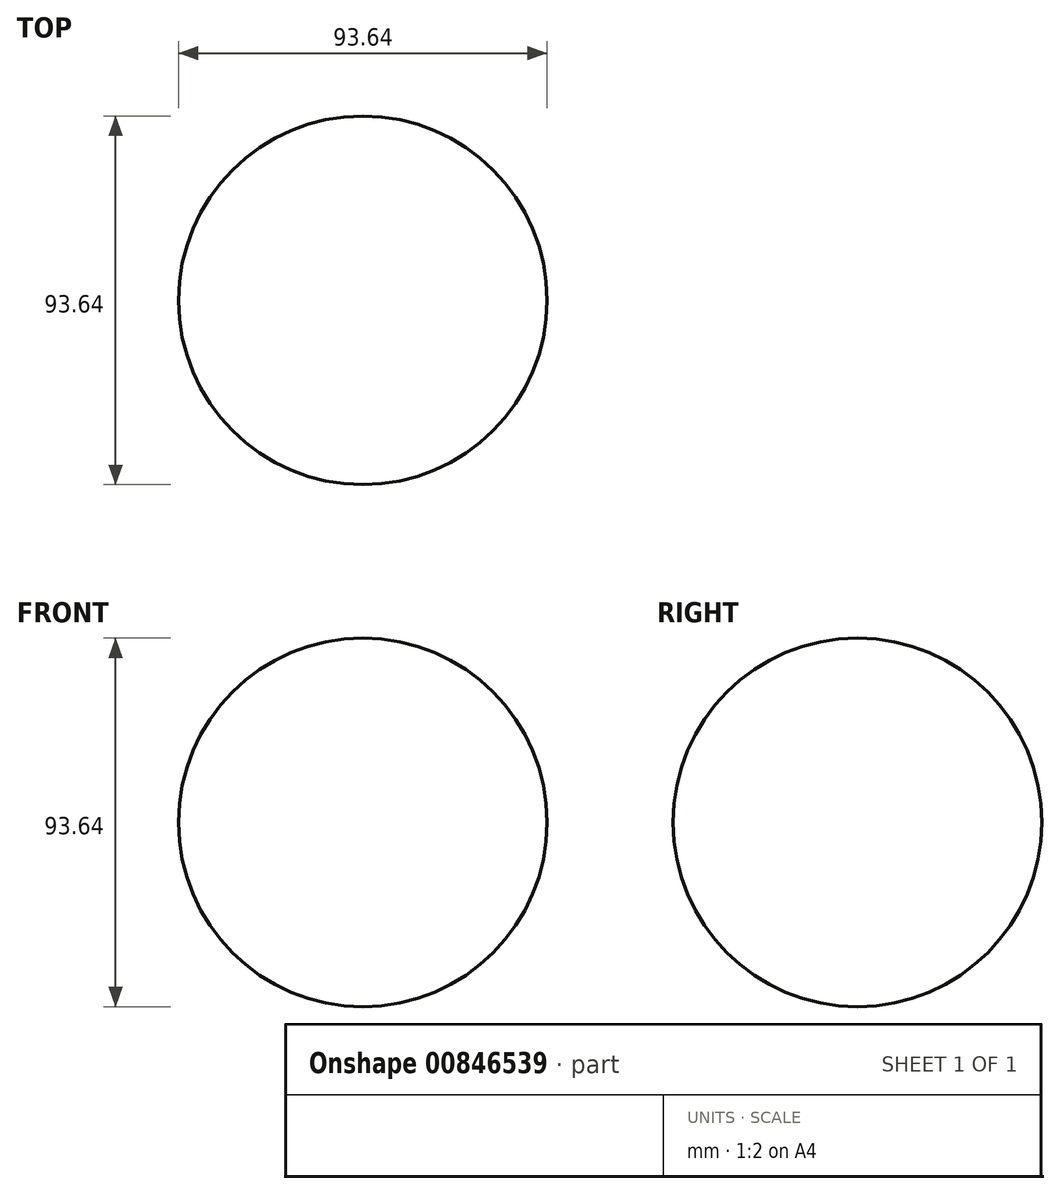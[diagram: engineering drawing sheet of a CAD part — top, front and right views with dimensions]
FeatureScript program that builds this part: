
annotation { "Feature Type Name" : "Feature", "Feature Type Description" : "" }
export const myFeature = defineFeature(function(context is Context, id is Id, definition is map)
    precondition{}
    {
        {
            var Q0;
            Q0=qCreatedBy(makeId("Front.planeOp"),FACE);
            var sketch = newSketch(context, id + "F0", { "sketchPlane" : qUnion([Q0])});
            skCircle(sketch, "E0", {"center": v(0, 0) * mm, "radius": 46.82 * mm});
            skLineSegment(sketch, "E1", {"start": v(0, 46.82) * mm, "end": v(0, -46.82) * mm});
            skSolve(sketch);
        }
        {
            var Q0;
            {var subQ0=sQuery(id+"F0.wireOp",EDGE,"E1");Q0=makeQuery(id+"F0.imprint","IMPRINT",FACE,{"disambiguationData":[TD([[makeQuery(id+"F0.imprint","IMPRINT",EDGE,{"derivedFrom":subQ0}),1.0]])]});}
            var Q1;
            Q1=sQuery(id+"F0.wireOp",EDGE,"E1");
            revolve(context, id + "F1", {"surfaceOperationType" : NewSurfaceOperationType.NEW, "entities" : qUnion([Q0]), "axis" : qUnion([Q1]), "revolveType" : RevolveType.FULL});
        }
    });
